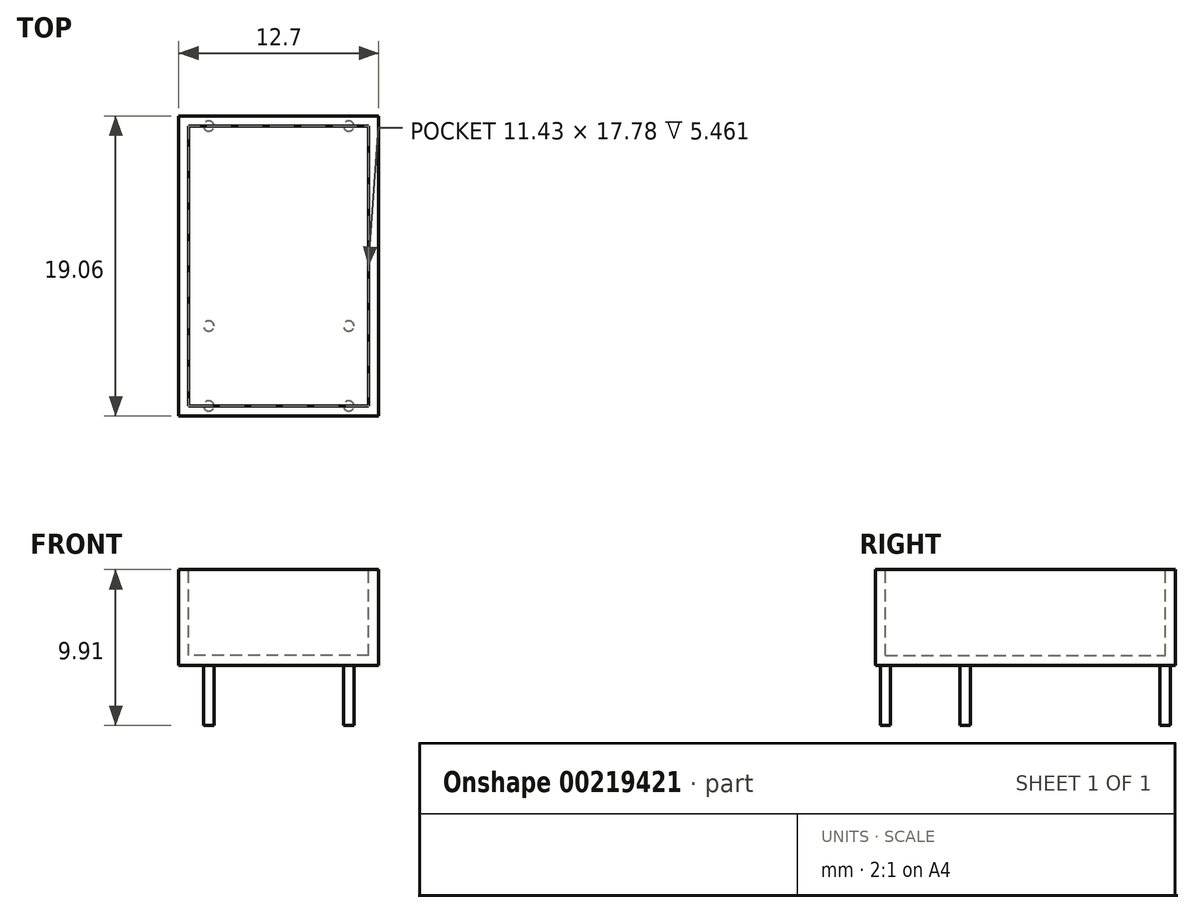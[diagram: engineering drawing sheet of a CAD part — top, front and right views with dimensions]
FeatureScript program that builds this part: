
annotation { "Feature Type Name" : "Feature", "Feature Type Description" : "" }
export const myFeature = defineFeature(function(context is Context, id is Id, definition is map)
    precondition{}
    {
        {
            assignVariable(context, id + "F0", {"variableType" : VariableType.LENGTH, "name" : "PinLen", "lengthValue" : 3.8 * mm});
        }
        {
            var Q0;
            Q0=qCreatedBy(makeId("Top.planeOp"),FACE);
            var sketch = newSketch(context, id + "F1", { "sketchPlane" : qUnion([Q0])});
            skLineSegment(sketch, "E0.bottom", {"start": v(6.35, -9.53) * mm, "end": v(-6.35, -9.53) * mm});
            skLineSegment(sketch, "E0.top", {"start": v(6.35, 9.53) * mm, "end": v(-6.35, 9.53) * mm});
            skLineSegment(sketch, "E0.left", {"start": v(6.35, -9.53) * mm, "end": v(6.35, 9.53) * mm});
            skLineSegment(sketch, "E0.right", {"start": v(-6.35, -9.53) * mm, "end": v(-6.35, 9.52) * mm});
            skPoint(sketch, "E0.middle", {"position": v(0, 0) * mm});
            skSolve(sketch);
        }
        {
            var Q0;
            Q0=makeQuery(id+"F1.imprint","IMPRINT",FACE,{"disambiguationData":[TD([[makeQuery(id+"F1.imprint","IMPRINT",EDGE,{"derivedFrom":sQuery(id+"F1.wireOp",EDGE,"E0.bottom")}),-1.0]])]});
            extrude(context, id + "F2", {"entities" : qUnion([Q0]), "depth" : 6.1 * mm, "offsetDistance" : 25.4 * mm});
        }
        {
            var Q0;
            Q0=makeQuery(id+"F2.opExtrude","CAP_FACE",FACE,{"disambiguationData":[OSD([sQuery(id+"F1.wireOp",EDGE,"E0.bottom"),sQuery(id+"F1.wireOp",EDGE,"E0.top"),sQuery(id+"F1.wireOp",EDGE,"E0.left"),sQuery(id+"F1.wireOp",EDGE,"E0.right")])],"isStart":false});
            var sketch = newSketch(context, id + "F3", { "sketchPlane" : qUnion([Q0])});
            skLineSegment(sketch, "E1.bottom", {"start": v(5.71, -8.9) * mm, "end": v(-5.72, -8.9) * mm});
            skLineSegment(sketch, "E1.top", {"start": v(5.72, 8.9) * mm, "end": v(-5.71, 8.9) * mm});
            skLineSegment(sketch, "E1.left", {"start": v(5.71, -8.9) * mm, "end": v(5.72, 8.9) * mm});
            skLineSegment(sketch, "E1.right", {"start": v(-5.72, -8.9) * mm, "end": v(-5.71, 8.89) * mm});
            skPoint(sketch, "E1.middle", {"position": v(0, 0) * mm});
            skSolve(sketch);
        }
        {
            var Q0;
            Q0=makeQuery(id+"F3.imprint","IMPRINT",FACE,{"disambiguationData":[TD([[makeQuery(id+"F3.imprint","IMPRINT",EDGE,{"derivedFrom":sQuery(id+"F3.wireOp",EDGE,"E1.bottom")}),-1.0]])]});
            extrude(context, id + "F4", {"entities" : qUnion([Q0]), "operationType" : NewBodyOperationType.REMOVE, "oppositeDirection" : true, "depth" : 5.46 * mm, "offsetDistance" : 25.4 * mm});
        }
        {
            var Q0;
            Q0=makeQuery(id+"F2.opExtrude","CAP_FACE",FACE,{"disambiguationData":[OSD([sQuery(id+"F1.wireOp",EDGE,"E0.bottom"),sQuery(id+"F1.wireOp",EDGE,"E0.top"),sQuery(id+"F1.wireOp",EDGE,"E0.left"),sQuery(id+"F1.wireOp",EDGE,"E0.right")])],"isStart":true});
            var sketch = newSketch(context, id + "F5", { "sketchPlane" : qUnion([Q0])});
            skCircle(sketch, "E2", {"center": v(4.45, -8.9) * mm, "radius": 0.33 * mm});
            skCircle(sketch, "E3", {"center": v(4.45, 3.81) * mm, "radius": 0.33 * mm});
            skCircle(sketch, "E4", {"center": v(4.45, 8.9) * mm, "radius": 0.33 * mm});
            skCircle(sketch, "E5.MirrorC", {"center": v(-4.45, 8.9) * mm, "radius": 0.33 * mm});
            skCircle(sketch, "E6.MirrorC", {"center": v(-4.45, 3.81) * mm, "radius": 0.33 * mm});
            skCircle(sketch, "E7.MirrorC", {"center": v(-4.45, -8.9) * mm, "radius": 0.33 * mm});
            skSolve(sketch);
        }
        {
            var Q0;
            Q0 = qSketchRegion(id + "F5", true);
            extrude(context, id + "F6", {"entities" : qUnion([Q0]), "depth" : getVariable(context, 'PinLen'), "offsetDistance" : 25.4 * mm});
        }
    });
